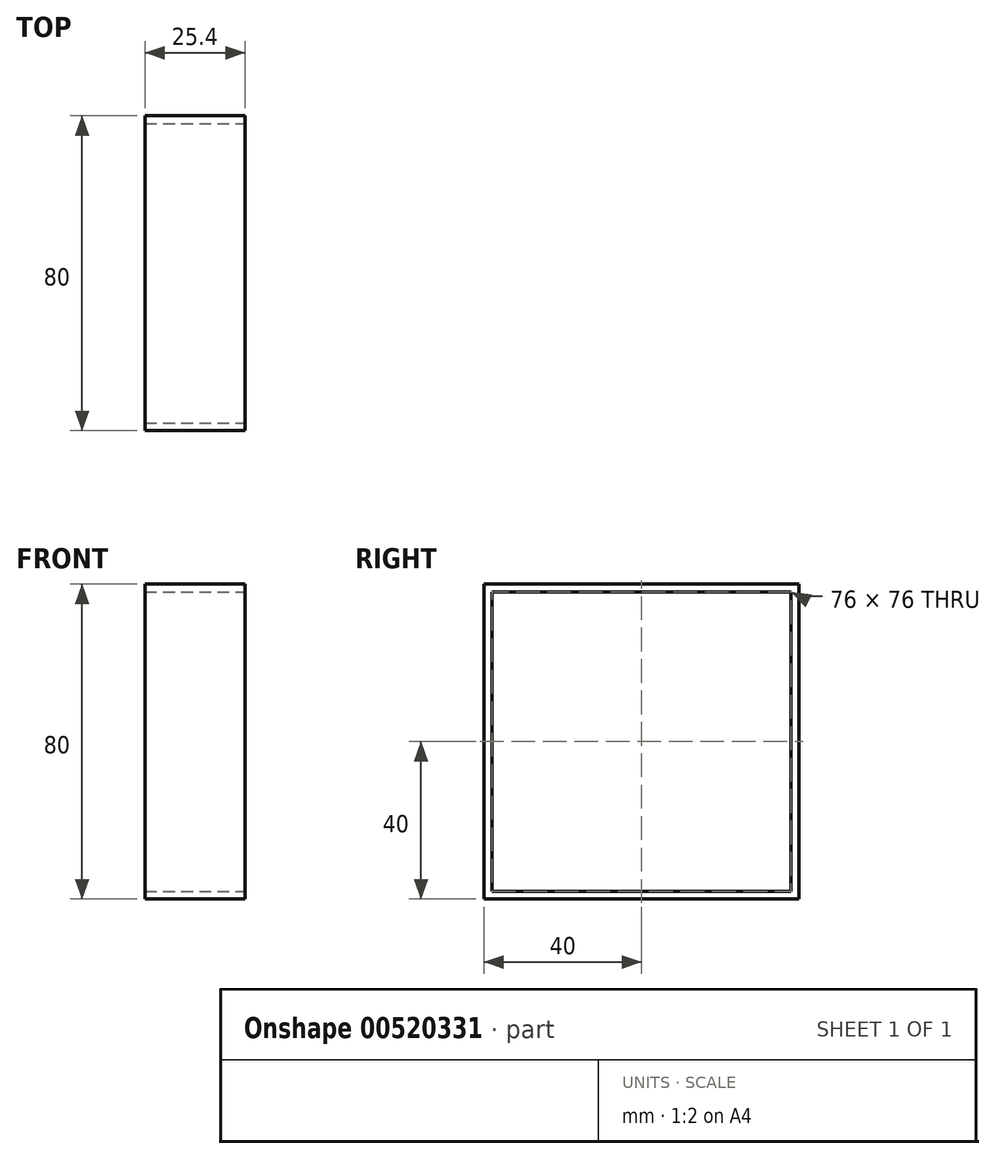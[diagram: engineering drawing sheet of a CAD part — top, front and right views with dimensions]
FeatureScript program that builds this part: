
annotation { "Feature Type Name" : "Feature", "Feature Type Description" : "" }
export const myFeature = defineFeature(function(context is Context, id is Id, definition is map)
    precondition{}
    {
        {
            var Q0;
            Q0=qCreatedBy(makeId("Right.planeOp"),FACE);
            var sketch = newSketch(context, id + "F0", { "sketchPlane" : qUnion([Q0])});
            skLineSegment(sketch, "E0.bottom", {"start": v(-40, 40) * mm, "end": v(40, 40) * mm});
            skLineSegment(sketch, "E0.top", {"start": v(-40, -40) * mm, "end": v(40, -40) * mm});
            skLineSegment(sketch, "E0.left", {"start": v(-40, 40) * mm, "end": v(-40, -40) * mm});
            skLineSegment(sketch, "E0.right", {"start": v(40, 40) * mm, "end": v(40, -40) * mm});
            skLineSegment(sketch, "E1.bottom", {"start": v(-38, 38) * mm, "end": v(38, 38) * mm});
            skLineSegment(sketch, "E1.top", {"start": v(-38, -38) * mm, "end": v(38, -38) * mm});
            skLineSegment(sketch, "E1.left", {"start": v(-38, 38) * mm, "end": v(-38, -38) * mm});
            skLineSegment(sketch, "E1.right", {"start": v(38, 38) * mm, "end": v(38, -38) * mm});
            skLineSegment(sketch, "E2.bottom", {"start": v(-34, 34) * mm, "end": v(34, 34) * mm});
            skLineSegment(sketch, "E2.top", {"start": v(-34, -34) * mm, "end": v(34, -34) * mm});
            skLineSegment(sketch, "E2.left", {"start": v(-34, 34) * mm, "end": v(-34, -34) * mm});
            skLineSegment(sketch, "E2.right", {"start": v(34, 34) * mm, "end": v(34, -34) * mm});
            skSolve(sketch);
        }
        {
            var Q0;
            Q0=makeQuery(id+"F0.imprint","IMPRINT",FACE,{"disambiguationData":[TD([[makeQuery(id+"F0.imprint","IMPRINT",EDGE,{"derivedFrom":sQuery(id+"F0.wireOp",EDGE,"E0.bottom")}),-1.0]])]});
            extrude(context, id + "F1", {"entities" : qUnion([Q0]), "oppositeDirection" : true, "depth" : 25.4 * mm, "offsetDistance" : 25.4 * mm});
        }
    });
